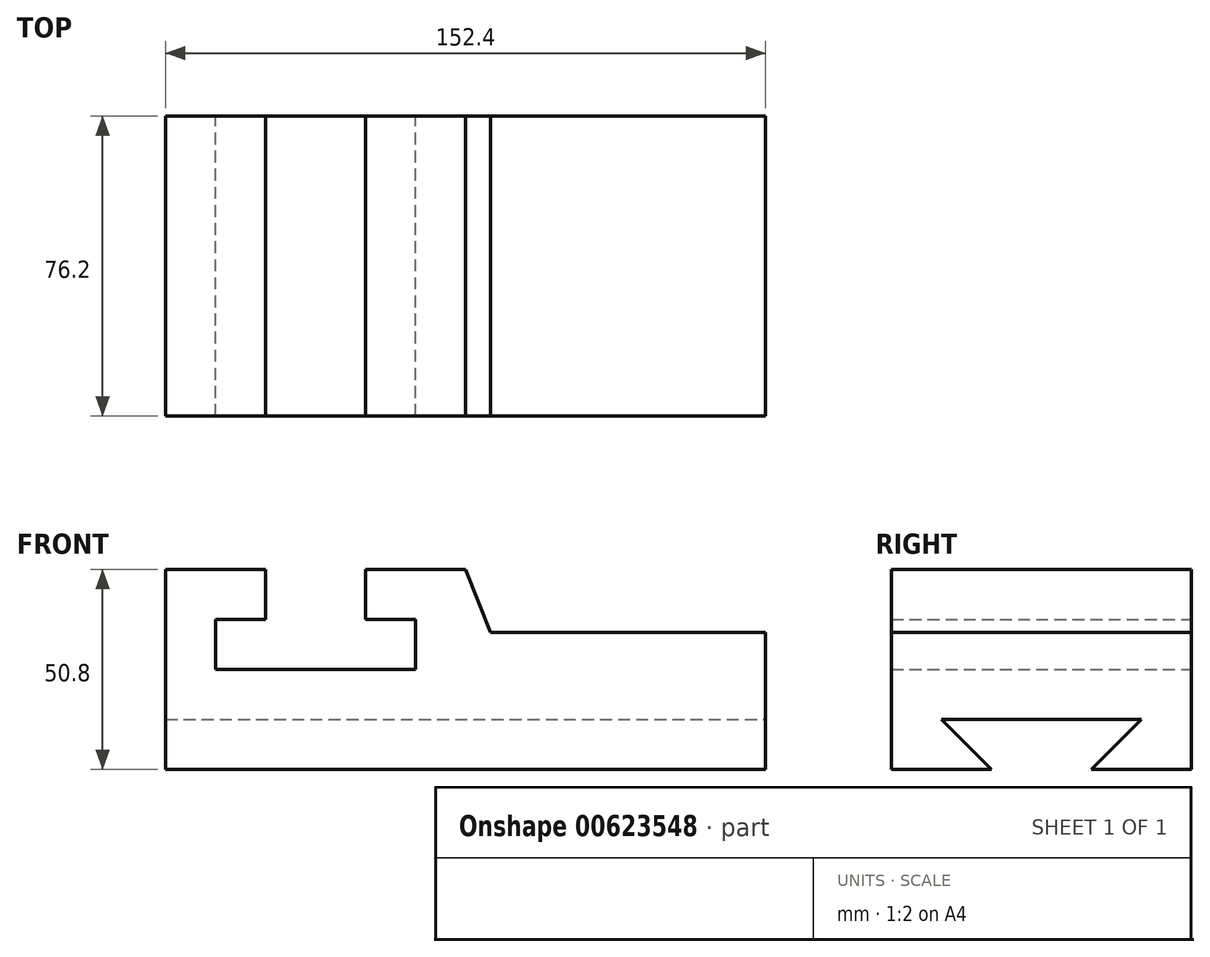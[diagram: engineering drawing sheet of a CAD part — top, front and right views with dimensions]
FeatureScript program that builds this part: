
annotation { "Feature Type Name" : "Feature", "Feature Type Description" : "" }
export const myFeature = defineFeature(function(context is Context, id is Id, definition is map)
    precondition{}
    {
        {
            var Q0;
            Q0=qCreatedBy(makeId("Front.planeOp"),FACE);
            var sketch = newSketch(context, id + "F0", { "sketchPlane" : qUnion([Q0])});
            skLineSegment(sketch, "E0", {"start": v(0, 0) * mm, "end": v(152.4, 0) * mm});
            skLineSegment(sketch, "E1", {"start": v(152.4, 0) * mm, "end": v(152.4, 34.77) * mm});
            skLineSegment(sketch, "E2", {"start": v(152.4, 34.77) * mm, "end": v(82.55, 34.77) * mm});
            skLineSegment(sketch, "E3", {"start": v(0, 0) * mm, "end": v(0, 50.8) * mm});
            skLineSegment(sketch, "E4", {"start": v(0, 50.8) * mm, "end": v(25.4, 50.8) * mm});
            skLineSegment(sketch, "E5", {"start": v(25.4, 50.8) * mm, "end": v(25.4, 38.1) * mm});
            skLineSegment(sketch, "E6", {"start": v(25.4, 38.1) * mm, "end": v(12.7, 38.1) * mm});
            skPoint(sketch, "E6.endSnap0", {"position": v(12.7, 50.8) * mm});
            skLineSegment(sketch, "E7", {"start": v(12.7, 38.1) * mm, "end": v(12.7, 25.4) * mm});
            skLineSegment(sketch, "E8", {"start": v(12.7, 25.4) * mm, "end": v(63.5, 25.4) * mm});
            skLineSegment(sketch, "E9", {"start": v(63.5, 25.4) * mm, "end": v(63.5, 38.1) * mm});
            skLineSegment(sketch, "E10", {"start": v(63.5, 38.1) * mm, "end": v(50.8, 38.1) * mm});
            skLineSegment(sketch, "E11", {"start": v(50.8, 38.1) * mm, "end": v(50.8, 50.8) * mm});
            skLineSegment(sketch, "E12", {"start": v(50.8, 50.8) * mm, "end": v(76.2, 50.8) * mm});
            skLineSegment(sketch, "E13", {"start": v(76.2, 50.8) * mm, "end": v(82.55, 34.77) * mm});
            skSolve(sketch);
        }
        {
            var Q0;
            Q0=makeQuery(id+"F0.imprint","IMPRINT",FACE,{"disambiguationData":[TD([[makeQuery(id+"F0.imprint","IMPRINT",EDGE,{"derivedFrom":sQuery(id+"F0.wireOp",EDGE,"E0")}),1.0]])]});
            extrude(context, id + "F1", {"entities" : qUnion([Q0]), "depth" : 76.2 * mm, "offsetDistance" : 25.4 * mm});
        }
        {
            var Q0;
            Q0=makeQuery(id+"F1.opExtrude","SWEPT_FACE",FACE,{"disambiguationData":[OSD([sQuery(id+"F0.wireOp",EDGE,"E1")])]});
            var sketch = newSketch(context, id + "F2", { "sketchPlane" : qUnion([Q0])});
            skLineSegment(sketch, "E14", {"start": v(-50.8, 0) * mm, "end": v(-25.4, 0) * mm});
            skLineSegment(sketch, "E15", {"start": v(-50.8, 0) * mm, "end": v(-38.1, 0) * mm});
            skLineSegment(sketch, "E16", {"start": v(-38.1, 12.7) * mm, "end": v(-12.7, 12.7) * mm});
            skLineSegment(sketch, "E17", {"start": v(-38.1, 12.7) * mm, "end": v(-63.5, 12.7) * mm});
            skLineSegment(sketch, "E18", {"start": v(-63.5, 12.7) * mm, "end": v(-50.8, 0) * mm});
            skLineSegment(sketch, "E19", {"start": v(-12.7, 12.7) * mm, "end": v(-25.4, 0) * mm});
            skSolve(sketch);
        }
        {
            var Q0;
            Q0=makeQuery(id+"F2.imprint","IMPRINT",FACE,{"disambiguationData":[TD([[makeQuery(id+"F2.imprint","IMPRINT",EDGE,{"derivedFrom":sQuery(id+"F2.wireOp",EDGE,"E14")}),1.0]])]});
            extrude(context, id + "F3", {"entities" : qUnion([Q0]), "operationType" : NewBodyOperationType.REMOVE, "oppositeDirection" : true, "depth" : 203.2 * mm, "offsetDistance" : 25.4 * mm});
        }
    });
